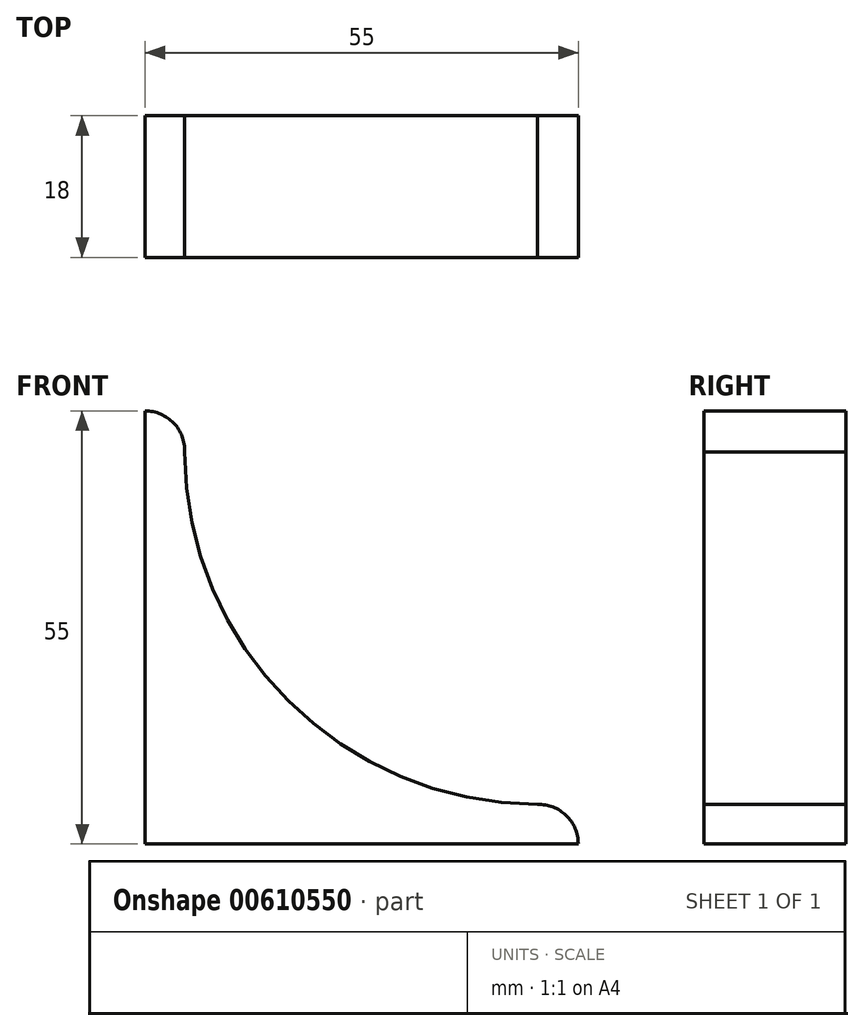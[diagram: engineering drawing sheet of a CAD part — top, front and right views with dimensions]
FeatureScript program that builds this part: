
annotation { "Feature Type Name" : "Feature", "Feature Type Description" : "" }
export const myFeature = defineFeature(function(context is Context, id is Id, definition is map)
    precondition{}
    {
        {
            var Q0;
            Q0=qCreatedBy(makeId("Front.planeOp"),FACE);
            var sketch = newSketch(context, id + "F0", { "sketchPlane" : qUnion([Q0])});
            skLineSegment(sketch, "E0", {"start": v(0, 0) * mm, "end": v(50, 0) * mm});
            skLineSegment(sketch, "E1", {"start": v(0, 0) * mm, "end": v(0, 50) * mm});
            skPoint(sketch, "E2.second.point", {"position": v(0, 50) * mm});
            skArc(sketch, "E3", {"start": v(5, 49.78) * mm, "mid": v(3.61, 53.46) * mm, "end": v(0, 55) * mm});
            skArc(sketch, "E4", {"start": v(55, 0) * mm, "mid": v(53.47, 3.6) * mm, "end": v(49.82, 5) * mm});
            skArc(sketch, "E5", {"start": v(5, 49.78) * mm, "mid": v(18.18, 18.15) * mm, "end": v(49.82, 5) * mm});
            skLineSegment(sketch, "E6", {"start": v(0, 50) * mm, "end": v(0, 55) * mm});
            skLineSegment(sketch, "E7", {"start": v(50, 0) * mm, "end": v(55, 0) * mm});
            skSolve(sketch);
        }
        {
            var Q0;
            Q0 = qSketchRegion(id + "F0", true);
            extrude(context, id + "F1", {"entities" : qUnion([Q0]), "depth" : 18 * mm, "offsetDistance" : 25 * mm});
        }
        {
            var Q0;
            Q0 = qSketchRegion(id + "F0", true);
            extrude(context, id + "F2", {"entities" : qUnion([Q0]), "operationType" : NewBodyOperationType.ADD, "depth" : 18 * mm, "offsetDistance" : 25 * mm});
        }
    });
